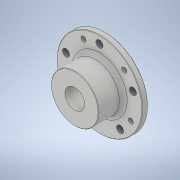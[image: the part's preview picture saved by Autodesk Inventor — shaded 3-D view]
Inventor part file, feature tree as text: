
AUTODESK INVENTOR PART (.ipt)
format: ipt  version: 2021 (Build 250183000, 183)  size: 216,064 bytes
history: native  units: in
note: dims shown in document units (in); Inventor stores cm internally (conversion verified against a paired STEP export)
features: thread x6, sketch x6, extrude x5, fillet x2, revolve x1, chamfer x1
ambient origin geometry x8: Origin, YZ Plane, XZ Plane, XY Plane, X Axis, Y Axis, Z Axis, Center Point
bodies: Solid1 (feature_tree)
feature tree (21):
  revolve  "Revolution1"  [1 undecoded]
  extrude  "Extrusion1"  Depth=0.36in
  extrude  "Extrusion2"  Depth=0.2in
  fillet  "Fillet1"  Radius=0.16in
  chamfer  "Chamfer1"  Distance=1.0in
  fillet  "Fillet2"  Radius=1.25in
  extrude  "Extrusion3"  Depth=0.25in TaperAngle=0.0deg
  thread  "Thread1"  [1 undecoded]
  thread  "Thread2"  [1 undecoded]
  thread  "Thread3"  [1 undecoded]
  thread  "Thread4"  [1 undecoded]
  thread  "Thread5"  [1 undecoded]
  thread  "Thread6"  [1 undecoded]
  extrude  "Extrusion4"  TaperAngle=45.0deg  [1 undecoded]
  extrude  "Extrusion5"  Depth=0.25in
  sketch  "Sketch1"  dims[d0=1.5in d1=1.56in]
  sketch  "Sketch2"  dims[d2=1.2in d3=0.36in]
  sketch  "Sketch3"  dims[d4=1.42in d5=0.2in d6=0.16in]
  sketch  "Sketch4"  dims[d7=0.52in]
  sketch  "Sketch5"  dims[d8=90.0deg]
  sketch  "Sketch6"  dims[d9=2.0in d10=1.0in d11=0.0in d12=1.25in d13=1.0in d14=0.0in d15=0.075in d16=0.03in d17=0.125in d18=45.0deg d19=0.25in d20=0.452in d21=0.48in d22=1.9685in d24=360.0deg d26=45.0deg d27=0.2in d28=0.2in d29=0.0in d30=0.435in d31=0.0in d32=0.435in d33=0.0in d34=0.435in d35=0.0in d36=0.435in d37=0.0in d38=0.435in d39=0.0in d40=0.435in d41=0.0in d42=1.0in d43=0.0in d44=0.325in d45=1.9685in d47=360.0deg d49=1.0in d50=0.0in]
note: 8 required parameter values undecoded (feature->parameter linkage not recoverable at this tier; creation-order binding heuristic only, values carry confidence <= 0.55)